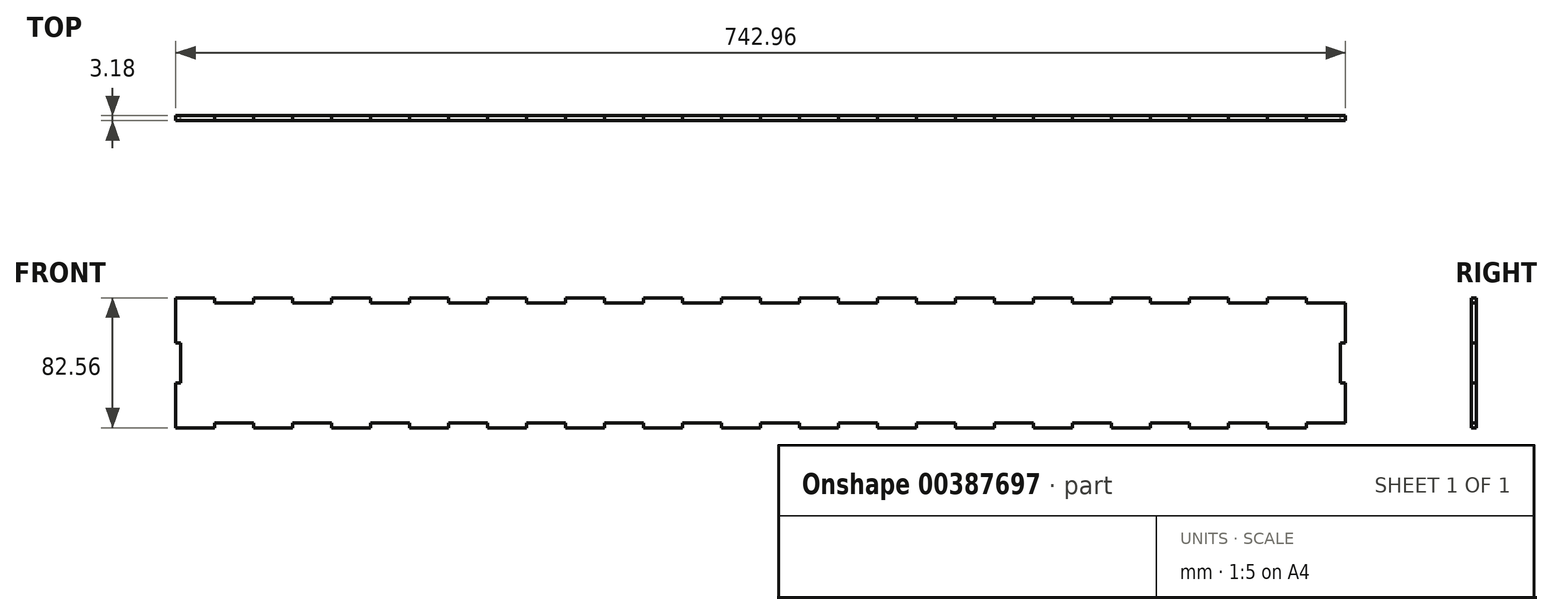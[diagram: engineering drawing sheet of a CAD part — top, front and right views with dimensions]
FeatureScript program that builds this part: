
annotation { "Feature Type Name" : "Feature", "Feature Type Description" : "" }
export const myFeature = defineFeature(function(context is Context, id is Id, definition is map)
    precondition{}
    {
        {
            var Q0;
            Q0=qCreatedBy(makeId("Front.planeOp"),FACE);
            var sketch = newSketch(context, id + "F0", { "sketchPlane" : qUnion([Q0])});
            skLineSegment(sketch, "E0.right", {"start": v(-371.48, -38.1) * mm, "end": v(-371.48, 38.1) * mm, "construction": true});
            skPoint(sketch, "E0.middle", {"position": v(0, 0) * mm});
            skPoint(sketch, "E1.middle", {"position": v(168.28, -6.35) * mm});
            skLineSegment(sketch, "E2.MirrorCS", {"start": v(123.83, 41.28) * mm, "end": v(123.83, 38.1) * mm});
            skLineSegment(sketch, "E3.MirrorCS", {"start": v(-247.65, 41.28) * mm, "end": v(-247.65, 38.1) * mm});
            skLineSegment(sketch, "E4.MirrorCS", {"start": v(272.42, 41.28) * mm, "end": v(272.42, 38.1) * mm});
            skLineSegment(sketch, "E5.MirrorCS", {"start": v(247.65, 41.28) * mm, "end": v(247.65, 38.1) * mm});
            skLineSegment(sketch, "E6.MirrorCS", {"start": v(-297.18, 41.28) * mm, "end": v(-297.18, 38.1) * mm});
            skLineSegment(sketch, "E7.MirrorCS", {"start": v(24.77, 41.28) * mm, "end": v(24.77, 38.1) * mm});
            skLineSegment(sketch, "E8.MirrorCS", {"start": v(-198.12, 41.28) * mm, "end": v(-198.12, 38.1) * mm});
            skLineSegment(sketch, "E9.MirrorCS", {"start": v(-49.53, 41.28) * mm, "end": v(-49.53, 38.1) * mm});
            skLineSegment(sketch, "E10.MirrorCS", {"start": v(222.89, 41.28) * mm, "end": v(222.89, 38.1) * mm});
            skLineSegment(sketch, "E11.MirrorCS", {"start": v(-74.3, 41.28) * mm, "end": v(-74.3, 38.1) * mm});
            skLineSegment(sketch, "E12.MirrorCS", {"start": v(-99.06, 41.28) * mm, "end": v(-99.06, 38.1) * mm});
            skLineSegment(sketch, "E13.MirrorCS", {"start": v(-148.59, 41.28) * mm, "end": v(-148.59, 38.1) * mm});
            skLineSegment(sketch, "E14.MirrorCS", {"start": v(-346.7, 41.28) * mm, "end": v(-346.7, 38.1) * mm});
            skLineSegment(sketch, "E15.MirrorCS", {"start": v(173.36, 41.28) * mm, "end": v(173.36, 38.1) * mm});
            skLineSegment(sketch, "E16.MirrorCS", {"start": v(-321.94, 41.28) * mm, "end": v(-321.94, 38.1) * mm});
            skLineSegment(sketch, "E17.MirrorCS", {"start": v(-123.82, 41.28) * mm, "end": v(-123.82, 38.1) * mm});
            skLineSegment(sketch, "E18.MirrorCS", {"start": v(-272.41, 41.28) * mm, "end": v(-272.41, 38.1) * mm});
            skLineSegment(sketch, "E19.MirrorCS", {"start": v(-173.35, 41.28) * mm, "end": v(-173.35, 38.1) * mm});
            skLineSegment(sketch, "E20.MirrorCS", {"start": v(198.12, 41.28) * mm, "end": v(198.12, 38.1) * mm});
            skLineSegment(sketch, "E21.MirrorCS", {"start": v(-24.76, 41.28) * mm, "end": v(-24.76, 38.1) * mm});
            skLineSegment(sketch, "E22.MirrorCS", {"start": v(74.3, 41.28) * mm, "end": v(74.3, 38.1) * mm});
            skLineSegment(sketch, "E23.MirrorCS", {"start": v(-222.88, 41.28) * mm, "end": v(-222.88, 38.1) * mm});
            skLineSegment(sketch, "E24.MirrorCS", {"start": v(346.71, 41.28) * mm, "end": v(346.71, 38.1) * mm});
            skLineSegment(sketch, "E25.MirrorCS", {"start": v(321.95, 41.28) * mm, "end": v(321.95, 38.1) * mm});
            skLineSegment(sketch, "E26.MirrorCS", {"start": v(297.18, 41.28) * mm, "end": v(297.18, 38.1) * mm});
            skLineSegment(sketch, "E27.MirrorCS", {"start": v(99.06, 41.28) * mm, "end": v(99.06, 38.1) * mm});
            skLineSegment(sketch, "E28.MirrorCS", {"start": v(148.6, 41.28) * mm, "end": v(148.6, 38.1) * mm});
            skLineSegment(sketch, "E29.MirrorCS", {"start": v(49.53, 41.28) * mm, "end": v(49.53, 38.1) * mm});
            skLineSegment(sketch, "E30.MirrorCS", {"start": v(0, 41.28) * mm, "end": v(0, 38.1) * mm});
            skLineSegment(sketch, "E31.MirrorCS", {"start": v(-272.41, 38.1) * mm, "end": v(-297.18, 38.1) * mm});
            skLineSegment(sketch, "E32.MirrorCS", {"start": v(-74.3, 38.1) * mm, "end": v(-99.06, 38.1) * mm});
            skLineSegment(sketch, "E33.MirrorCS", {"start": v(173.36, 38.1) * mm, "end": v(148.6, 38.1) * mm});
            skLineSegment(sketch, "E34.MirrorCS", {"start": v(-148.59, 41.28) * mm, "end": v(-173.35, 41.28) * mm});
            skLineSegment(sketch, "E35.MirrorCS", {"start": v(272.42, 38.1) * mm, "end": v(247.65, 38.1) * mm});
            skLineSegment(sketch, "E36.MirrorCS", {"start": v(24.77, 38.1) * mm, "end": v(0, 38.1) * mm});
            skLineSegment(sketch, "E37.MirrorCS", {"start": v(-198.12, 41.28) * mm, "end": v(-222.88, 41.28) * mm});
            skLineSegment(sketch, "E38.MirrorCS", {"start": v(-173.35, 38.1) * mm, "end": v(-198.12, 38.1) * mm});
            skLineSegment(sketch, "E39.MirrorCS", {"start": v(-24.76, 38.1) * mm, "end": v(-49.53, 38.1) * mm});
            skLineSegment(sketch, "E40.MirrorCS", {"start": v(222.89, 38.1) * mm, "end": v(198.12, 38.1) * mm});
            skLineSegment(sketch, "E41.MirrorCS", {"start": v(74.3, 38.1) * mm, "end": v(49.53, 38.1) * mm});
            skLineSegment(sketch, "E42.MirrorCS", {"start": v(-222.88, 38.1) * mm, "end": v(-247.65, 38.1) * mm});
            skLineSegment(sketch, "E43.MirrorCS", {"start": v(148.6, 41.28) * mm, "end": v(123.83, 41.28) * mm});
            skLineSegment(sketch, "E44.MirrorCS", {"start": v(99.06, 41.28) * mm, "end": v(74.3, 41.28) * mm});
            skLineSegment(sketch, "E45.MirrorCS", {"start": v(0, 41.28) * mm, "end": v(-24.76, 41.28) * mm});
            skLineSegment(sketch, "E46.MirrorCS", {"start": v(-99.06, 41.28) * mm, "end": v(-123.82, 41.28) * mm});
            skLineSegment(sketch, "E47.MirrorCS", {"start": v(123.83, 38.1) * mm, "end": v(99.06, 38.1) * mm});
            skLineSegment(sketch, "E48.MirrorCS", {"start": v(-297.18, 41.28) * mm, "end": v(-321.94, 41.28) * mm});
            skLineSegment(sketch, "E49.MirrorCS", {"start": v(198.12, 41.28) * mm, "end": v(173.36, 41.28) * mm});
            skLineSegment(sketch, "E50.MirrorCS", {"start": v(49.53, 41.28) * mm, "end": v(24.77, 41.28) * mm});
            skLineSegment(sketch, "E51.MirrorCS", {"start": v(-321.94, 38.1) * mm, "end": v(-346.7, 38.1) * mm});
            skLineSegment(sketch, "E52.MirrorCS", {"start": v(-123.82, 38.1) * mm, "end": v(-148.59, 38.1) * mm});
            skLineSegment(sketch, "E53.MirrorCS", {"start": v(346.71, 41.28) * mm, "end": v(321.95, 41.28) * mm});
            skLineSegment(sketch, "E54.MirrorCS", {"start": v(321.95, 38.1) * mm, "end": v(297.18, 38.1) * mm});
            skLineSegment(sketch, "E55.MirrorCS", {"start": v(297.18, 41.28) * mm, "end": v(272.42, 41.28) * mm});
            skLineSegment(sketch, "E56.MirrorCS", {"start": v(-49.53, 41.28) * mm, "end": v(-74.3, 41.28) * mm});
            skLineSegment(sketch, "E57.MirrorCS", {"start": v(-247.65, 41.28) * mm, "end": v(-272.41, 41.28) * mm});
            skLineSegment(sketch, "E58.MirrorCS", {"start": v(247.65, 41.28) * mm, "end": v(222.89, 41.28) * mm});
            skLineSegment(sketch, "E59.MirrorCS", {"start": v(346.71, 38.1) * mm, "end": v(371.48, 38.1) * mm});
            skLineSegment(sketch, "E60.MirrorCS", {"start": v(-346.7, 41.28) * mm, "end": v(-371.47, 41.28) * mm});
            skLineSegment(sketch, "E61", {"start": v(-371.47, 41.28) * mm, "end": v(-371.48, 38.1) * mm});
            skLineSegment(sketch, "E62.top", {"start": v(371.48, -12.7) * mm, "end": v(368.3, -12.7) * mm});
            skLineSegment(sketch, "E62.left", {"start": v(371.48, -38.1) * mm, "end": v(371.48, -12.7) * mm});
            skLineSegment(sketch, "E63.bottom", {"start": v(368.3, -12.7) * mm, "end": v(371.48, -12.7) * mm});
            skLineSegment(sketch, "E63.top", {"start": v(368.3, 12.7) * mm, "end": v(371.48, 12.7) * mm});
            skLineSegment(sketch, "E63.left", {"start": v(368.3, -12.7) * mm, "end": v(368.3, 12.7) * mm});
            skLineSegment(sketch, "E64.bottom", {"start": v(371.48, 12.7) * mm, "end": v(368.3, 12.7) * mm});
            skLineSegment(sketch, "E64.top", {"start": v(371.48, 38.1) * mm, "end": v(368.3, 38.1) * mm});
            skLineSegment(sketch, "E64.left", {"start": v(371.48, 12.7) * mm, "end": v(371.48, 38.1) * mm});
            skLineSegment(sketch, "E65.MirrorCS", {"start": v(-371.48, -38.1) * mm, "end": v(-371.48, -12.7) * mm});
            skLineSegment(sketch, "E66.MirrorCS", {"start": v(-368.3, -12.7) * mm, "end": v(-371.48, -12.7) * mm});
            skLineSegment(sketch, "E67.MirrorCS", {"start": v(-368.3, -12.7) * mm, "end": v(-368.3, 12.7) * mm});
            skLineSegment(sketch, "E68.MirrorCS", {"start": v(-368.3, 12.7) * mm, "end": v(-371.48, 12.7) * mm});
            skLineSegment(sketch, "E69", {"start": v(-371.48, 12.7) * mm, "end": v(-371.48, 38.1) * mm});
            skLineSegment(sketch, "E70.MirrorCS", {"start": v(198.12, -41.28) * mm, "end": v(198.12, -38.1) * mm});
            skLineSegment(sketch, "E71.MirrorCS", {"start": v(272.41, -41.28) * mm, "end": v(272.41, -38.1) * mm});
            skLineSegment(sketch, "E72.MirrorCS", {"start": v(-74.3, -41.28) * mm, "end": v(-74.3, -38.1) * mm});
            skLineSegment(sketch, "E73.MirrorCS", {"start": v(99.06, -41.28) * mm, "end": v(99.06, -38.1) * mm});
            skLineSegment(sketch, "E74.MirrorCS", {"start": v(148.59, -41.28) * mm, "end": v(123.82, -41.28) * mm});
            skLineSegment(sketch, "E75.MirrorCS", {"start": v(346.7, -41.28) * mm, "end": v(321.94, -41.28) * mm});
            skLineSegment(sketch, "E76.MirrorCS", {"start": v(-198.12, -41.28) * mm, "end": v(-222.89, -41.28) * mm});
            skLineSegment(sketch, "E77.MirrorCS", {"start": v(-24.77, -41.28) * mm, "end": v(-24.77, -38.1) * mm});
            skLineSegment(sketch, "E78.MirrorCS", {"start": v(-198.12, -41.28) * mm, "end": v(-198.12, -38.1) * mm});
            skLineSegment(sketch, "E79.MirrorCS", {"start": v(0, -41.28) * mm, "end": v(0, -38.1) * mm});
            skLineSegment(sketch, "E80.MirrorCS", {"start": v(-99.06, -41.28) * mm, "end": v(-123.83, -41.28) * mm});
            skLineSegment(sketch, "E81.MirrorCS", {"start": v(-346.71, -41.28) * mm, "end": v(-346.71, -38.1) * mm});
            skLineSegment(sketch, "E82.MirrorCS", {"start": v(24.76, -41.28) * mm, "end": v(24.76, -38.1) * mm});
            skLineSegment(sketch, "E83.MirrorCS", {"start": v(247.65, -41.28) * mm, "end": v(247.65, -38.1) * mm});
            skLineSegment(sketch, "E84.MirrorCS", {"start": v(198.12, -41.28) * mm, "end": v(173.35, -41.28) * mm});
            skLineSegment(sketch, "E85.MirrorCS", {"start": v(-49.53, -41.28) * mm, "end": v(-74.3, -41.28) * mm});
            skLineSegment(sketch, "E86.MirrorCS", {"start": v(-222.89, -41.28) * mm, "end": v(-222.89, -38.1) * mm});
            skLineSegment(sketch, "E87.MirrorCS", {"start": v(-321.95, -41.28) * mm, "end": v(-321.95, -38.1) * mm});
            skLineSegment(sketch, "E88.MirrorCS", {"start": v(-123.83, -41.28) * mm, "end": v(-123.83, -38.1) * mm});
            skLineSegment(sketch, "E89.MirrorCS", {"start": v(-99.06, -41.28) * mm, "end": v(-99.06, -38.1) * mm});
            skLineSegment(sketch, "E90.MirrorCS", {"start": v(148.59, -41.28) * mm, "end": v(148.59, -38.1) * mm});
            skLineSegment(sketch, "E91.MirrorCS", {"start": v(0, -41.28) * mm, "end": v(-24.77, -41.28) * mm});
            skLineSegment(sketch, "E92.MirrorCS", {"start": v(49.53, -41.28) * mm, "end": v(49.53, -38.1) * mm});
            skLineSegment(sketch, "E93.MirrorCS", {"start": v(-173.36, -41.28) * mm, "end": v(-173.36, -38.1) * mm});
            skLineSegment(sketch, "E94.MirrorCS", {"start": v(-297.18, -41.28) * mm, "end": v(-297.18, -38.1) * mm});
            skLineSegment(sketch, "E95.MirrorCS", {"start": v(-247.65, -41.28) * mm, "end": v(-272.42, -41.28) * mm});
            skLineSegment(sketch, "E96.MirrorCS", {"start": v(346.7, -41.28) * mm, "end": v(346.7, -38.1) * mm});
            skLineSegment(sketch, "E97.MirrorCS", {"start": v(123.82, -41.28) * mm, "end": v(123.82, -38.1) * mm});
            skLineSegment(sketch, "E98.MirrorCS", {"start": v(-148.6, -41.28) * mm, "end": v(-148.6, -38.1) * mm});
            skLineSegment(sketch, "E99.MirrorCS", {"start": v(-247.65, -41.28) * mm, "end": v(-247.65, -38.1) * mm});
            skLineSegment(sketch, "E100.MirrorCS", {"start": v(49.53, -41.28) * mm, "end": v(24.76, -41.28) * mm});
            skLineSegment(sketch, "E101.MirrorCS", {"start": v(74.3, -41.28) * mm, "end": v(74.3, -38.1) * mm});
            skLineSegment(sketch, "E102.MirrorCS", {"start": v(173.35, -41.28) * mm, "end": v(173.35, -38.1) * mm});
            skLineSegment(sketch, "E103.MirrorCS", {"start": v(-272.42, -41.28) * mm, "end": v(-272.42, -38.1) * mm});
            skLineSegment(sketch, "E104.MirrorCS", {"start": v(-148.6, -41.28) * mm, "end": v(-173.36, -41.28) * mm});
            skLineSegment(sketch, "E105.MirrorCS", {"start": v(-297.18, -41.28) * mm, "end": v(-321.95, -41.28) * mm});
            skLineSegment(sketch, "E106.MirrorCS", {"start": v(222.88, -41.28) * mm, "end": v(222.88, -38.1) * mm});
            skLineSegment(sketch, "E107.MirrorCS", {"start": v(-49.53, -41.28) * mm, "end": v(-49.53, -38.1) * mm});
            skLineSegment(sketch, "E108.MirrorCS", {"start": v(297.18, -41.28) * mm, "end": v(297.18, -38.1) * mm});
            skLineSegment(sketch, "E109.MirrorCS", {"start": v(297.18, -41.28) * mm, "end": v(272.41, -41.28) * mm});
            skLineSegment(sketch, "E110.MirrorCS", {"start": v(321.94, -41.28) * mm, "end": v(321.94, -38.1) * mm});
            skLineSegment(sketch, "E111.MirrorCS", {"start": v(-346.71, -41.28) * mm, "end": v(-371.48, -41.28) * mm});
            skLineSegment(sketch, "E112.MirrorCS", {"start": v(24.76, -38.1) * mm, "end": v(0, -38.1) * mm});
            skLineSegment(sketch, "E113.MirrorCS", {"start": v(-123.83, -38.1) * mm, "end": v(-148.6, -38.1) * mm});
            skLineSegment(sketch, "E114.MirrorCS", {"start": v(346.7, -38.1) * mm, "end": v(371.47, -38.1) * mm});
            skLineSegment(sketch, "E115.MirrorCS", {"start": v(123.82, -38.1) * mm, "end": v(99.06, -38.1) * mm});
            skLineSegment(sketch, "E116.MirrorCS", {"start": v(-272.42, -38.1) * mm, "end": v(-297.18, -38.1) * mm});
            skLineSegment(sketch, "E117.MirrorCS", {"start": v(-173.36, -38.1) * mm, "end": v(-198.12, -38.1) * mm});
            skLineSegment(sketch, "E118.MirrorCS", {"start": v(222.88, -38.1) * mm, "end": v(198.12, -38.1) * mm});
            skLineSegment(sketch, "E119.MirrorCS", {"start": v(173.35, -38.1) * mm, "end": v(148.59, -38.1) * mm});
            skLineSegment(sketch, "E120.MirrorCS", {"start": v(272.41, -38.1) * mm, "end": v(247.65, -38.1) * mm});
            skLineSegment(sketch, "E121.MirrorCS", {"start": v(-321.95, -38.1) * mm, "end": v(-346.71, -38.1) * mm});
            skLineSegment(sketch, "E122.MirrorCS", {"start": v(74.3, -38.1) * mm, "end": v(49.53, -38.1) * mm});
            skLineSegment(sketch, "E123.MirrorCS", {"start": v(321.94, -38.1) * mm, "end": v(297.18, -38.1) * mm});
            skLineSegment(sketch, "E124.MirrorCS", {"start": v(-222.89, -38.1) * mm, "end": v(-247.65, -38.1) * mm});
            skLineSegment(sketch, "E125.MirrorCS", {"start": v(-24.77, -38.1) * mm, "end": v(-49.53, -38.1) * mm});
            skLineSegment(sketch, "E126.MirrorCS", {"start": v(-74.3, -38.1) * mm, "end": v(-99.06, -38.1) * mm});
            skLineSegment(sketch, "E127", {"start": v(-371.48, -38.1) * mm, "end": v(-371.48, -41.28) * mm});
            skLineSegment(sketch, "E128", {"start": v(244.47, -41.28) * mm, "end": v(247.65, -41.28) * mm});
            skLineSegment(sketch, "E129", {"start": v(92.07, -41.28) * mm, "end": v(74.3, -41.28) * mm});
            skLineSegment(sketch, "E130", {"start": v(92.07, -41.28) * mm, "end": v(99.06, -41.28) * mm});
            skLineSegment(sketch, "E131", {"start": v(222.88, -41.28) * mm, "end": v(244.47, -41.28) * mm});
            skSolve(sketch);
        }
        {
            var Q0;
            Q0=qSketchRegion(id+"F0",true);
            extrude(context, id + "F1", {"entities" : qUnion([Q0]), "depth" : 3.17 * mm});
        }
    });
